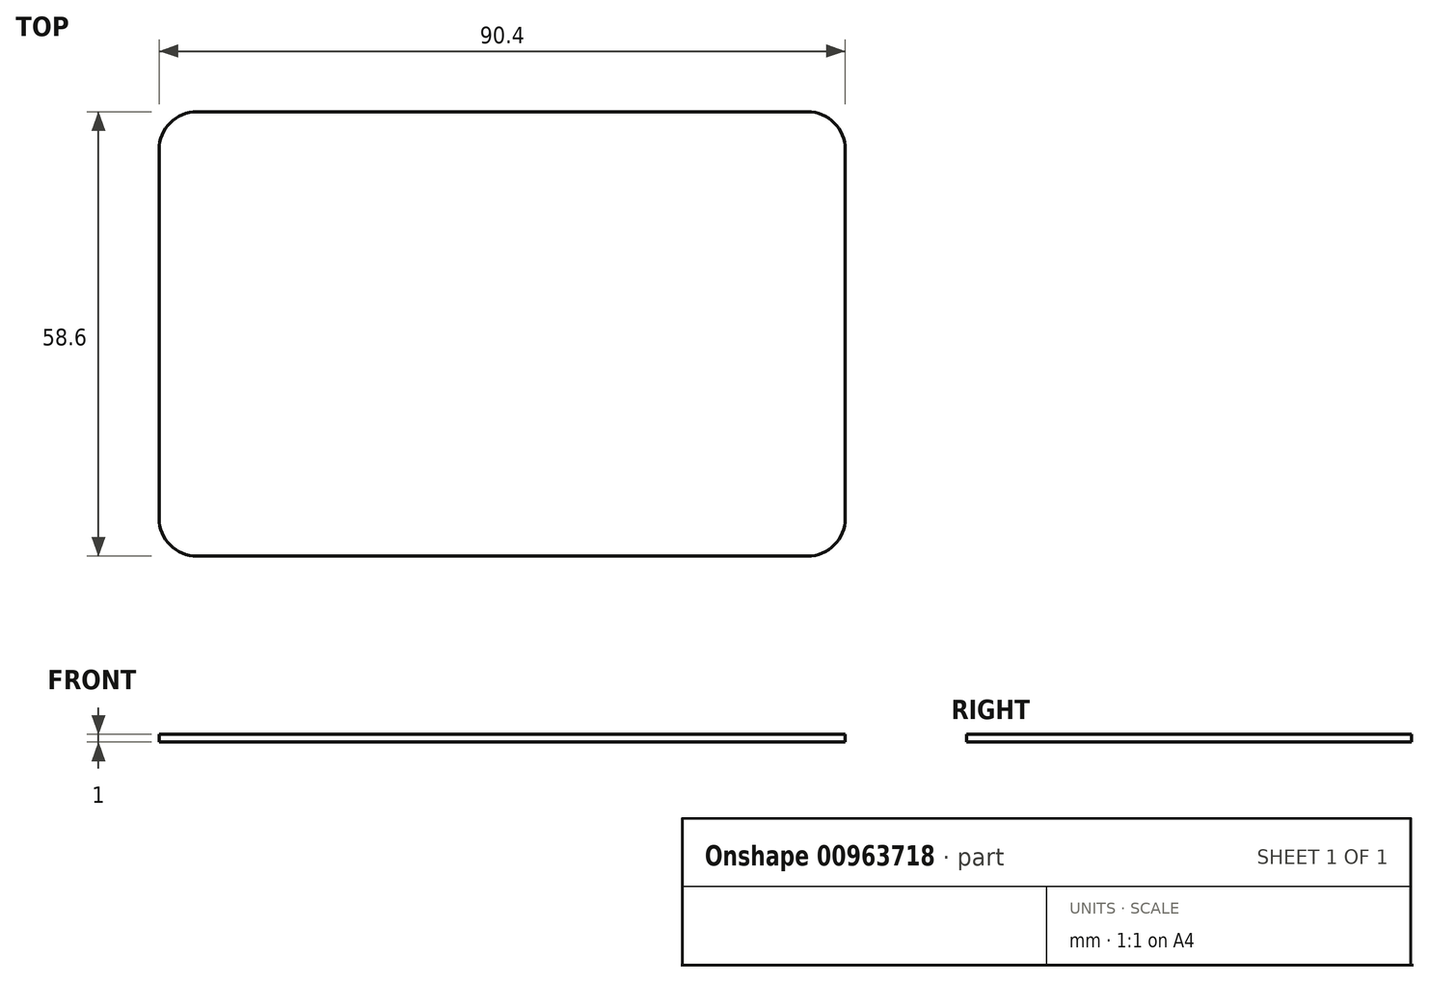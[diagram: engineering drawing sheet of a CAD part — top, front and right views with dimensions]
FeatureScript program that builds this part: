
annotation { "Feature Type Name" : "Feature", "Feature Type Description" : "" }
export const myFeature = defineFeature(function(context is Context, id is Id, definition is map)
    precondition{}
    {
        {
            var Q0;
            Q0=qCreatedBy(makeId("Top.planeOp"),FACE);
            var sketch = newSketch(context, id + "F0", { "sketchPlane" : qUnion([Q0])});
            skLineSegment(sketch, "E0.bottom", {"start": v(5, 0) * mm, "end": v(85.4, 0) * mm});
            skLineSegment(sketch, "E0.top", {"start": v(5, 58.6) * mm, "end": v(85.4, 58.6) * mm});
            skLineSegment(sketch, "E0.left", {"start": v(0, 5) * mm, "end": v(0, 53.6) * mm});
            skLineSegment(sketch, "E0.right", {"start": v(90.4, 5) * mm, "end": v(90.4, 53.6) * mm});
            skArc(sketch, "E1", {"start": v(5, 58.6) * mm, "mid": v(1.46, 57.14) * mm, "end": v(0, 53.6) * mm});
            skArc(sketch, "E2", {"start": v(0, 5) * mm, "mid": v(1.46, 1.46) * mm, "end": v(5, 0) * mm});
            skArc(sketch, "E3", {"start": v(85.4, 0) * mm, "mid": v(88.94, 1.46) * mm, "end": v(90.4, 5) * mm});
            skArc(sketch, "E4", {"start": v(90.4, 53.6) * mm, "mid": v(88.94, 57.14) * mm, "end": v(85.4, 58.6) * mm});
            skSolve(sketch);
        }
        {
            var Q0;
            Q0=makeQuery(id+"F0.imprint","IMPRINT",FACE,{"disambiguationData":[TD([[makeQuery(id+"F0.imprint","IMPRINT",EDGE,{"derivedFrom":sQuery(id+"F0.wireOp",EDGE,"E0.bottom")}),1.0]])]});
            extrude(context, id + "F1", {"entities" : qUnion([Q0]), "depth" : 1 * mm, "offsetDistance" : 25 * mm});
        }
    });
